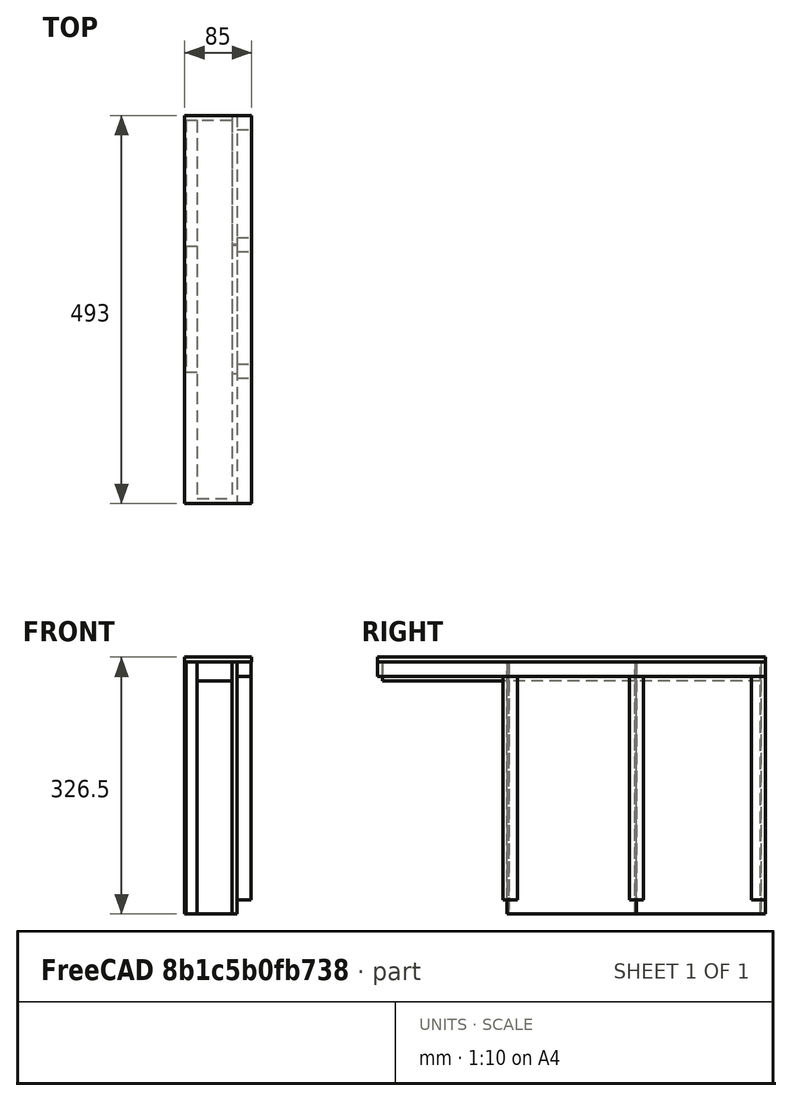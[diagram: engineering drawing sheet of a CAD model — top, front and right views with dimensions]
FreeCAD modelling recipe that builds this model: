
FCSTD DOCUMENT  (FreeCAD 0.21R33694 (Git))
Label: enclosure
License: All rights reserved
LicenseURL: http://en.wikipedia.org/wiki/All_rights_reserved
objects: PartDesign::Body×18, TechDraw::DrawViewDimension×12, PartDesign::FeatureBase×11, Sketcher::SketchObject×7, PartDesign::Pad×7, TechDraw::DrawViewPart×6, TechDraw::DrawSVGTemplate×1, TechDraw::DrawProjGroupItem×1, TechDraw::DrawProjGroup×1, TechDraw::DrawPage×1
note: 64 computed .brp shape members not serialized (recipe doc carries the construction recipe); baked Part::Feature solids carry a one-line shape summary decoded from their .brp

FEATURE [Sketcher::SketchObject] Sketch
  FullyConstrained = true
  MapMode = 5
  Placement = pos=(0,0,0) rot=(1,0,0;1.5708rad)
  Support = -> [XZ_Plane]
  sketch-geometry (6):
    g0: LineSegment StartX=0 StartY=2e-16 StartZ=0 EndX=14 EndY=2e-16 EndZ=0
    g1: LineSegment StartX=14 StartY=320 StartZ=0 EndX=0 EndY=320 EndZ=0
    g2: LineSegment StartX=0 StartY=320 StartZ=0 EndX=0 EndY=0 EndZ=0
    g3: LineSegment StartX=14 StartY=2e-16 StartZ=0 EndX=14 EndY=24 EndZ=0
    g4: LineSegment StartX=14 StartY=24 StartZ=0 EndX=14 EndY=296 EndZ=0
    g5: LineSegment StartX=14 StartY=296 StartZ=0 EndX=14 EndY=320 EndZ=0
  constraints (17):
    c: Coincident(g0,g3)
    c: Coincident(g5,g1)
    c: Coincident(g1,g2)
    c: Coincident(g2,g0)
    c: Horizontal(g0)
    c: Horizontal(g1)
    c: Vertical(g2)
    c: DistanceX(g0,g0) = 14
    c: DistanceY(g3,g5) = 320
    c: Coincident(g0,g-1)
    c: Coincident(g3,g4)
    c: Vertical(g3)
    c: Distance(g3,g0) = 24
    c: Coincident(g4,g5)
    c: Vertical(g4)
    c: Vertical(g5)
    c: Distance(g4,g1) = 24
FEATURE [PartDesign::Pad] Pad
  Direction = (0,-1,-2e-16)
  Length = 160
  Length2 = 10
  Placement = pos=(0,0,0) rot=(1,0,0;1.5708rad)
  Profile = -> Sketch
  ReferenceAxis = -> Sketch [N_Axis]
  Type = 0
FEATURE [PartDesign::Body] Body  label="p10panel_1"
  Group = -> [Sketch,Pad]
  Origin = -> Origin
  Placement = pos=(0,0,-0.5) rot=(0,0,1;0rad)
  Tip = -> Pad
FEATURE [PartDesign::FeatureBase] Clone
  BaseFeature = -> Body
FEATURE [PartDesign::Body] Body001  label="p10panel_2"
  Group = -> [Clone]
  Origin = -> Origin001
  Placement = pos=(0,160,-0.5) rot=(0,0,1;0rad)
  Tip = -> Clone
FEATURE [PartDesign::FeatureBase] Clone001
  BaseFeature = -> Body
FEATURE [PartDesign::Body] Body002  label="p10panel_3"
  Group = -> [Clone001]
  Origin = -> Origin002
  Placement = pos=(0,320,-0.5) rot=(0,0,1;0rad)
  Tip = -> Clone001
FEATURE [Sketcher::SketchObject] Sketch001
  FullyConstrained = true
  MapMode = 5
  Placement = pos=(0,0,0) rot=(1,0,0;1.5708rad)
  Support = -> [XZ_Plane003]
  sketch-geometry (4):
    g0: LineSegment StartX=0 StartY=0 StartZ=0 EndX=44 EndY=0 EndZ=0
    g1: LineSegment StartX=44 StartY=0 StartZ=0 EndX=44 EndY=24 EndZ=0
    g2: LineSegment StartX=44 StartY=24 StartZ=0 EndX=0 EndY=24 EndZ=0
    g3: LineSegment StartX=0 StartY=24 StartZ=0 EndX=0 EndY=0 EndZ=0
  constraints (11):
    c: Coincident(g0,g1)
    c: Coincident(g1,g2)
    c: Coincident(g2,g3)
    c: Coincident(g3,g0)
    c: Horizontal(g0)
    c: Horizontal(g2)
    c: Vertical(g1)
    c: Vertical(g3)
    c: DistanceX(g0,g0) = 44
    c: DistanceY(g1,g1) = 24
    c: Coincident(g0,g-1)
FEATURE [PartDesign::Pad] Pad001
  Direction = (0,-1,-2e-16)
  Length = 480
  Length2 = 10
  Placement = pos=(0,0,0) rot=(1,0,0;1.5708rad)
  Profile = -> Sketch001
  ReferenceAxis = -> Sketch001 [N_Axis]
  Type = 0
FEATURE [PartDesign::Body] Body003  label="bottomEdge"
  Group = -> [Sketch001,Pad001]
  Origin = -> Origin003
  Placement = pos=(14,319.5,-0.5) rot=(0,0,1;0rad)
  Tip = -> Pad001
FEATURE [PartDesign::FeatureBase] Clone002
  BaseFeature = -> Body003
  Placement = pos=(14,-166.5,296) rot=(0,0,1;0rad)
FEATURE [PartDesign::Body] Body004  label="topEdge"
  Group = -> [Clone002]
  Origin = -> Origin004
  Placement = pos=(0,486,-0.5) rot=(0,0,1;0rad)
  Tip = -> Clone002
FEATURE [Sketcher::SketchObject] Sketch002
  FullyConstrained = true
  MapMode = 5
  Placement = pos=(0,0,0) rot=(1,0,0;1.5708rad)
  Support = -> [XZ_Plane005]
  sketch-geometry (14):
    g0: LineSegment StartX=85 StartY=-6.5 StartZ=0 EndX=85 EndY=0 EndZ=0
    g1: LineSegment StartX=0 StartY=0 StartZ=0 EndX=0 EndY=-6.5 EndZ=0
    g2: LineSegment StartX=0 StartY=-6.5 StartZ=0 EndX=16 EndY=-6.5 EndZ=0
    g3: LineSegment StartX=16 StartY=0 StartZ=0 EndX=0 EndY=0 EndZ=0
    g4: LineSegment StartX=66.5 StartY=0 StartZ=0 EndX=60 EndY=0 EndZ=0
    g5: LineSegment StartX=85 StartY=0 StartZ=0 EndX=84.5 EndY=0 EndZ=0
    g6: LineSegment StartX=84.5 StartY=0 StartZ=0 EndX=66.5 EndY=0 EndZ=0
    g7: LineSegment StartX=84.5 StartY=-6.5 StartZ=0 EndX=85 EndY=-6.5 EndZ=0
    g8: LineSegment StartX=66.5 StartY=-6.5 StartZ=0 EndX=84.5 EndY=-6.5 EndZ=0
    g9: LineSegment StartX=60 StartY=-6.5 StartZ=0 EndX=66.5 EndY=-6.5 EndZ=0
    g10: LineSegment StartX=60 StartY=0 StartZ=0 EndX=42 EndY=0 EndZ=0
    g11: LineSegment StartX=42 StartY=0 StartZ=0 EndX=16 EndY=0 EndZ=0
    g12: LineSegment StartX=16 StartY=-6.5 StartZ=0 EndX=42 EndY=-6.5 EndZ=0
    g13: LineSegment StartX=42 StartY=-6.5 StartZ=0 EndX=60 EndY=-6.5 EndZ=0
  constraints (41):
    c: Coincident(g7,g0)
    c: Coincident(g0,g5)
    c: Coincident(g3,g1)
    c: Coincident(g1,g2)
    c: Vertical(g0)
    c: Vertical(g1)
    c: DistanceY(g0,g0) = 6.5
    c: Coincident(g3,g-1)
    c: DistanceX(g2,g7) = 85
    c: Coincident(g2,g12)
    c: Horizontal(g2)
    c: Horizontal(g3)
    c: Distance(g1,g2) = 16
    c: Distance(g1,g11) = 16
    c: Coincident(g4,g10)
    c: Coincident(g6,g4)
    c: Horizontal(g4)
    c: Coincident(g5,g6)
    c: Horizontal(g5)
    c: Horizontal(g6)
    c: Coincident(g8,g7)
    c: Horizontal(g7)
    c: Coincident(g9,g8)
    c: Horizontal(g8)
    c: Coincident(g13,g9)
    c: Horizontal(g9)
    c: Distance(g13,g8) = 6.5
    c: Horizontal(g10)
    c: Horizontal(g11)
    c: Coincident(g12,g13)
    c: Horizontal(g12)
    c: Horizontal(g13)
    c: Distance(g12,g9) = 18
    c: Distance(g3,g10) = 26
    c: Coincident(g3,g11)
    c: Coincident(g11,g10)
    c: Distance(g10,g4) = 18
    c: Distance(g4,g4) = 6.5
    c: Distance(g4,g5) = 18
    c: Distance(g2,g12) = 26
    c: Distance(g8,g7) = 18
FEATURE [PartDesign::Pad] Pad002
  Direction = (0,-1,-2e-16)
  Length = 493
  Length2 = 10
  Placement = pos=(0,0,0) rot=(1,0,0;1.5708rad)
  Profile = -> Sketch002
  ReferenceAxis = -> Sketch002 [N_Axis]
  Type = 0
FEATURE [PartDesign::Body] Body005  label="bottom"
  Group = -> [Sketch002,Pad002]
  Origin = -> Origin005
  Placement = pos=(-2,326,-0.5) rot=(0,0,1;0rad)
  Tip = -> Pad002
FEATURE [Sketcher::SketchObject] Sketch003
  FullyConstrained = true
  MapMode = 5
  Placement = pos=(0,0,0) rot=(1,0,0;1.5708rad)
  Support = -> [XZ_Plane006]
  sketch-geometry (8):
    g0: LineSegment StartX=60 StartY=0 StartZ=0 EndX=60 EndY=320 EndZ=0
    g1: LineSegment StartX=0 StartY=320 StartZ=0 EndX=0 EndY=0 EndZ=0
    g2: LineSegment StartX=16 StartY=0 StartZ=0 EndX=60 EndY=0 EndZ=0
    g3: LineSegment StartX=0 StartY=0 StartZ=0 EndX=2 EndY=0 EndZ=0
    g4: LineSegment StartX=2 StartY=0 StartZ=0 EndX=16 EndY=0 EndZ=0
    g5: LineSegment StartX=60 StartY=320 StartZ=0 EndX=16 EndY=320 EndZ=0
    g6: LineSegment StartX=16 StartY=320 StartZ=0 EndX=2 EndY=320 EndZ=0
    g7: LineSegment StartX=2 StartY=320 StartZ=0 EndX=0 EndY=320 EndZ=0
  constraints (23):
    c: Coincident(g2,g0)
    c: Coincident(g0,g5)
    c: Coincident(g7,g1)
    c: Coincident(g1,g3)
    c: Vertical(g0)
    c: Vertical(g1)
    c: DistanceX(g3,g2) = 60
    c: DistanceY(g0,g0) = 320
    c: Coincident(g3,g-1)
    c: Coincident(g4,g2)
    c: Horizontal(g2)
    c: Distance(g1,g4) = 16
    c: Coincident(g3,g4)
    c: Horizontal(g3)
    c: Horizontal(g4)
    c: Distance(g3,g1) = 2
    c: Coincident(g5,g6)
    c: Horizontal(g5)
    c: Coincident(g6,g7)
    c: Horizontal(g6)
    c: Horizontal(g7)
    c: Distance(g5,g1) = 16
    c: Distance(g6,g1) = 2
FEATURE [PartDesign::Pad] Pad003
  Direction = (0,-1,-2e-16)
  Length = 6.5
  Length2 = 10
  Placement = pos=(0,0,0) rot=(1,0,0;1.5708rad)
  Profile = -> Sketch003
  ReferenceAxis = -> Sketch003 [N_Axis]
  Type = 0
FEATURE [PartDesign::Body] Body006  label="rightSide"
  Group = -> [Sketch003,Pad003]
  Origin = -> Origin006
  Placement = pos=(-2,-160.5,-0.5) rot=(0,0,1;0rad)
  Tip = -> Pad003
FEATURE [PartDesign::FeatureBase] Clone003
  BaseFeature = -> Body006
  Placement = pos=(-2,-160,3.6e-14) rot=(0,0,1;0rad)
FEATURE [PartDesign::Body] Body007  label="leftSide"
  Group = -> [Clone003]
  Origin = -> Origin007
  Placement = pos=(0,486,-0.5) rot=(0,0,1;0rad)
  Tip = -> Clone003
FEATURE [PartDesign::FeatureBase] Clone004
  BaseFeature = -> Body005
  Placement = pos=(-2,326,-7.2e-14) rot=(0,0,1;0rad)
FEATURE [PartDesign::Body] Body008  label="top"
  Group = -> [Clone004]
  Origin = -> Origin008
  Placement = pos=(0,2.8e-14,326) rot=(0,0,1;0rad)
  Tip = -> Clone004
FEATURE [Sketcher::SketchObject] Sketch004
  FullyConstrained = true
  MapMode = 5
  Placement = pos=(0,0,0) rot=(1,0,0;1.5708rad)
  Support = -> [XZ_Plane009]
  sketch-geometry (4):
    g0: LineSegment StartX=0 StartY=0 StartZ=0 EndX=6.5 EndY=0 EndZ=0
    g1: LineSegment StartX=6.5 StartY=0 StartZ=0 EndX=6.5 EndY=320 EndZ=0
    g2: LineSegment StartX=6.5 StartY=320 StartZ=0 EndX=0 EndY=320 EndZ=0
    g3: LineSegment StartX=0 StartY=320 StartZ=0 EndX=0 EndY=0 EndZ=0
  constraints (11):
    c: Coincident(g0,g1)
    c: Coincident(g1,g2)
    c: Coincident(g2,g3)
    c: Coincident(g3,g0)
    c: Horizontal(g0)
    c: Horizontal(g2)
    c: Vertical(g1)
    c: Vertical(g3)
    c: DistanceX(g0,g0) = 6.5
    c: DistanceY(g1,g1) = 320
    c: Coincident(g0,g-1)
FEATURE [PartDesign::Pad] Pad004
  Direction = (0,-1,-2e-16)
  Length = 164.33
  Length2 = 10
  Placement = pos=(0,0,0) rot=(1,0,0;1.5708rad)
  Profile = -> Sketch004
  ReferenceAxis = -> Sketch004 [N_Axis]
  Type = 0
FEATURE [PartDesign::Body] Body009  label="back_1"
  Group = -> [Sketch004,Pad004]
  Origin = -> Origin009
  Placement = pos=(58,-2.5,-0.5) rot=(0,0,1;0rad)
  Tip = -> Pad004
FEATURE [PartDesign::FeatureBase] Clone005
  BaseFeature = -> Body009
  Placement = pos=(58,-6.2,0) rot=(0,0,1;0rad)
FEATURE [PartDesign::Body] Body010  label="back_2"
  Group = -> [Clone005]
  Origin = -> Origin010
  Placement = pos=(122.5,168,319.5) rot=(0,-1,0;3.14159rad)
  Tip = -> Clone005
FEATURE [PartDesign::FeatureBase] Clone006
  BaseFeature = -> Body009
  Placement = pos=(58,-6,1e-15) rot=(0,0,1;0rad)
FEATURE [PartDesign::Body] Body011  label="back_3"
  Group = -> [Clone006]
  Origin = -> Origin011
  Placement = pos=(-2.81e-14,332,-0.5) rot=(0,0,1;0rad)
  Tip = -> Clone006
FEATURE [Sketcher::SketchObject] Sketch005
  FullyConstrained = true
  MapMode = 5
  Placement = pos=(0,0,0) rot=(1,0,0;1.5708rad)
  Support = -> [XZ_Plane012]
  sketch-geometry (4):
    g0: LineSegment StartX=0 StartY=0 StartZ=0 EndX=18 EndY=0 EndZ=0
    g1: LineSegment StartX=18 StartY=0 StartZ=0 EndX=18 EndY=18 EndZ=0
    g2: LineSegment StartX=18 StartY=18 StartZ=0 EndX=0 EndY=18 EndZ=0
    g3: LineSegment StartX=0 StartY=18 StartZ=0 EndX=0 EndY=0 EndZ=0
  constraints (11):
    c: Coincident(g0,g1)
    c: Coincident(g1,g2)
    c: Coincident(g2,g3)
    c: Coincident(g3,g0)
    c: Horizontal(g0)
    c: Horizontal(g2)
    c: Vertical(g1)
    c: Vertical(g3)
    c: DistanceX(g0,g0) = 18
    c: DistanceY(g1,g1) = 18
    c: Coincident(g0,g-1)
FEATURE [PartDesign::Pad] Pad005
  Direction = (0,-1,-2e-16)
  Length = 493
  Length2 = 10
  Placement = pos=(0,0,0) rot=(1,0,0;1.5708rad)
  Profile = -> Sketch005
  ReferenceAxis = -> Sketch005 [N_Axis]
  Type = 0
FEATURE [PartDesign::Body] Body012  label="bottomBackEdge"
  Group = -> [Sketch005,Pad005]
  Origin = -> Origin012
  Placement = pos=(64.5,326,-0.5) rot=(0,0,1;0rad)
  Tip = -> Pad005
FEATURE [PartDesign::FeatureBase] Clone007
  BaseFeature = -> Body012
  Placement = pos=(64.5,326,0) rot=(0,0,1;0rad)
FEATURE [PartDesign::Body] Body013  label="topBackEdge"
  Group = -> [Clone007]
  Origin = -> Origin013
  Placement = pos=(0,0,301.5) rot=(0,0,1;0rad)
  Tip = -> Clone007
FEATURE [Sketcher::SketchObject] Sketch006
  FullyConstrained = true
  MapMode = 5
  Placement = pos=(0,0,0) rot=(1,0,0;1.5708rad)
  Support = -> [XZ_Plane014]
  sketch-geometry (4):
    g0: LineSegment StartX=0 StartY=284 StartZ=0 EndX=18 EndY=284 EndZ=0
    g1: LineSegment StartX=18 StartY=284 StartZ=0 EndX=18 EndY=0 EndZ=0
    g2: LineSegment StartX=18 StartY=0 StartZ=0 EndX=0 EndY=0 EndZ=0
    g3: LineSegment StartX=0 StartY=0 StartZ=0 EndX=0 EndY=284 EndZ=0
  constraints (11):
    c: Coincident(g0,g1)
    c: Coincident(g1,g2)
    c: Coincident(g2,g3)
    c: Coincident(g3,g0)
    c: Horizontal(g0)
    c: Horizontal(g2)
    c: Vertical(g1)
    c: Vertical(g3)
    c: DistanceX(g2,g2) = 18
    c: DistanceY(g1,g1) = 284
    c: Coincident(g-1,g2)
FEATURE [PartDesign::Pad] Pad006
  Direction = (0,-1,2e-16)
  Length = 18
  Length2 = 10
  Placement = pos=(0,0,0) rot=(1,0,0;1.5708rad)
  Profile = -> Sketch006
  ReferenceAxis = -> Sketch006 [N_Axis]
  Type = 0
FEATURE [PartDesign::Body] Body014  label="rightBackEdge"
  Group = -> [Sketch006,Pad006]
  Origin = -> Origin014
  Placement = pos=(64.5,-149,17.5) rot=(0,0,1;0rad)
  Tip = -> Pad006
FEATURE [PartDesign::FeatureBase] Clone008
  BaseFeature = -> Body014
  Placement = pos=(64.5,-148,17.5) rot=(0,0,1;0rad)
FEATURE [PartDesign::Body] Body015  label="leftBackEdge"
  Group = -> [Clone008]
  Origin = -> Origin015
  Placement = pos=(0,474,0) rot=(0,0,1;0rad)
  Tip = -> Clone008
FEATURE [TechDraw::DrawSVGTemplate] Template
  Height = 297
  Orientation = 0
  Template = <path>
  Width = 210
FEATURE [TechDraw::DrawProjGroupItem] ProjItem  label="Front"
  CoarseView = false
  Direction = (-0.57735,0.57735,0.57735)
  Focus = 100
  HardHidden = false
  IsoCount = 0
  IsoHidden = false
  IsoVisible = false
  LockPosition = true
  Perspective = false
  Rotation = 0
  RotationVector = (-0.707107,-0.707107,0)
  Scale = 0.2
  ScaleType = 2
  ScrubCount = 0
  SeamHidden = false
  SeamVisible = false
  SmoothHidden = false
  SmoothVisible = true
  Source = -> [Body015,Body,Body001,Body002,Body003,Body004,Body005,Body006,Body007,Body008,Body009,Body010,Body011,Body012,Body013,Body014]
  Type = 0
  X = 0
  XDirection = (-0.707107,-0.707107,0)
  Y = 0
FEATURE [TechDraw::DrawProjGroup] ProjGroup
  Anchor = -> ProjItem
  AutoDistribute = true
  LockPosition = false
  ProjectionType = 0
  Rotation = 0
  Scale = 0.2
  ScaleType = 2
  Source = -> [Body015,Body,Body001,Body002,Body003,Body004,Body005,Body006,Body007,Body008,Body009,Body010,Body011,Body012,Body013,Body014]
  Views = -> [ProjItem]
  X = 60
  Y = 241
  spacingX = 15
  spacingY = 15
FEATURE [TechDraw::DrawViewPart] View001  label="2x left/right panel"
  CoarseView = false
  Direction = (0,1,0)
  Focus = 100
  HardHidden = false
  IsoCount = 0
  IsoHidden = false
  IsoVisible = false
  LockPosition = false
  Perspective = false
  Rotation = 0
  Scale = 0.25
  ScaleType = 2
  ScrubCount = 0
  SeamHidden = false
  SeamVisible = false
  SmoothHidden = false
  SmoothVisible = true
  Source = -> [Body007]
  X = 155
  XDirection = (-1,0,0)
  Y = 51
FEATURE [TechDraw::DrawViewPart] View002  label="2x bottom/top panel"
  CoarseView = false
  Direction = (0,0,1)
  Focus = 100
  HardHidden = false
  IsoCount = 0
  IsoHidden = false
  IsoVisible = false
  LockPosition = false
  Perspective = false
  Rotation = 0
  Scale = 0.25
  ScaleType = 2
  ScrubCount = 0
  SeamHidden = false
  SeamVisible = false
  SmoothHidden = false
  SmoothVisible = true
  Source = -> [Body008]
  X = 155
  XDirection = (1,0,0)
  Y = 223
FEATURE [TechDraw::DrawViewPart] View004  label="3x back panel"
  CoarseView = false
  Direction = (1,0,0)
  Focus = 100
  HardHidden = false
  IsoCount = 0
  IsoHidden = false
  IsoVisible = false
  LockPosition = false
  Perspective = false
  Rotation = 0
  Scale = 0.25
  ScaleType = 2
  ScrubCount = 0
  SeamHidden = false
  SeamVisible = false
  SmoothHidden = false
  SmoothVisible = true
  Source = -> [Body009]
  X = 55
  XDirection = (0,1,0)
  Y = 51
FEATURE [TechDraw::DrawViewDimension] Dimension003
  AngleOverride = false
  Arbitrary = false
  ArbitraryTolerances = false
  EqualTolerance = true
  ExtensionAngle = 0
  FormatSpec = %.2w
  FormatSpecOverTolerance = %+.2w
  FormatSpecUnderTolerance = %+.2w
  Inverted = false
  LineAngle = 0
  LockPosition = false
  MeasureType = 1
  OverTolerance = 0
  References2D = -> [View002]
  Rotation = 0
  ScaleType = 1
  TheoreticalExact = false
  Type = 1
  UnderTolerance = 0
  X = -0.495893
  Y = 71.1127
FEATURE [TechDraw::DrawViewDimension] Dimension004
  AngleOverride = false
  Arbitrary = false
  ArbitraryTolerances = false
  EqualTolerance = true
  ExtensionAngle = 0
  FormatSpec = %.2w
  FormatSpecOverTolerance = %+.2w
  FormatSpecUnderTolerance = %+.2w
  Inverted = false
  LineAngle = 0
  LockPosition = false
  MeasureType = 1
  OverTolerance = 0
  References2D = -> [View001]
  Rotation = 0
  ScaleType = 1
  TheoreticalExact = false
  Type = 1
  UnderTolerance = 0
  X = -0.512282
  Y = 48.5031
FEATURE [TechDraw::DrawViewDimension] Dimension006
  AngleOverride = false
  Arbitrary = false
  ArbitraryTolerances = false
  EqualTolerance = true
  ExtensionAngle = 0
  FormatSpec = %.2w
  FormatSpecOverTolerance = %+.2w
  FormatSpecUnderTolerance = %+.2w
  Inverted = false
  LineAngle = 0
  LockPosition = false
  MeasureType = 1
  OverTolerance = 0
  References2D = -> [View004]
  Rotation = 0
  ScaleType = 1
  TheoreticalExact = false
  Type = 1
  UnderTolerance = 0
  X = -3.9584
  Y = 48.9458
FEATURE [TechDraw::DrawViewPart] View  label="2x bottom/top backEdge"
  CoarseView = false
  Direction = (1,0,0)
  Focus = 100
  HardHidden = false
  IsoCount = 0
  IsoHidden = false
  IsoVisible = false
  LockPosition = false
  Perspective = false
  Rotation = 0
  Scale = 0.25
  ScaleType = 2
  ScrubCount = 0
  SeamHidden = false
  SeamVisible = false
  SmoothHidden = false
  SmoothVisible = true
  Source = -> [Body012]
  X = 90
  XDirection = (0,1,0)
  Y = 143
FEATURE [TechDraw::DrawViewPart] View005  label="4x left/right/middleLeft/middleRight backEdge"
  CoarseView = false
  Direction = (1,0,0)
  Focus = 100
  HardHidden = false
  IsoCount = 0
  IsoHidden = false
  IsoVisible = false
  LockPosition = false
  Perspective = false
  Rotation = 90
  Scale = 0.25
  ScaleType = 2
  ScrubCount = 0
  SeamHidden = false
  SeamVisible = false
  SmoothHidden = false
  SmoothVisible = true
  Source = -> [Body014]
  X = 64
  XDirection = (0,1,0)
  Y = 170
  expr: Rotation = 90 °
FEATURE [TechDraw::DrawViewDimension] Dimension008
  AngleOverride = false
  Arbitrary = false
  ArbitraryTolerances = false
  EqualTolerance = true
  ExtensionAngle = 0
  FormatSpec = %.2w
  FormatSpecOverTolerance = %+.2w
  FormatSpecUnderTolerance = %+.2w
  Inverted = false
  LineAngle = 0
  LockPosition = false
  MeasureType = 1
  OverTolerance = 0
  References2D = -> [View005]
  Rotation = 0
  ScaleType = 1
  TheoreticalExact = false
  Type = 1
  UnderTolerance = 0
  X = -3.06326
  Y = 10.904
FEATURE [TechDraw::DrawViewDimension] Dimension010
  AngleOverride = false
  Arbitrary = false
  ArbitraryTolerances = false
  EqualTolerance = true
  ExtensionAngle = 0
  FormatSpec = %.2w
  FormatSpecOverTolerance = %+.2w
  FormatSpecUnderTolerance = %+.2w
  Inverted = false
  LineAngle = 0
  LockPosition = false
  MeasureType = 1
  OverTolerance = 0
  References2D = -> [View]
  Rotation = 0
  ScaleType = 1
  TheoreticalExact = false
  Type = 1
  UnderTolerance = 0
  X = -0.859065
  Y = 11.3821
FEATURE [TechDraw::DrawViewPart] View006  label="2x bottom/top edge"
  CoarseView = false
  Direction = (1,0,0)
  Focus = 100
  HardHidden = false
  IsoCount = 0
  IsoHidden = false
  IsoVisible = false
  LockPosition = false
  Perspective = false
  Rotation = 0
  Scale = 0.25
  ScaleType = 2
  ScrubCount = 0
  SeamHidden = false
  SeamVisible = false
  SmoothHidden = false
  SmoothVisible = true
  Source = -> [Body003]
  X = 88
  XDirection = (0,1,0)
  Y = 118
FEATURE [TechDraw::DrawViewDimension] Dimension012
  AngleOverride = false
  Arbitrary = false
  ArbitraryTolerances = false
  EqualTolerance = true
  ExtensionAngle = 0
  FormatSpec = %.2w
  FormatSpecOverTolerance = %+.2w
  FormatSpecUnderTolerance = %+.2w
  Inverted = false
  LineAngle = 0
  LockPosition = false
  MeasureType = 1
  OverTolerance = 0
  References2D = -> [View006]
  Rotation = 0
  ScaleType = 1
  TheoreticalExact = false
  Type = 1
  UnderTolerance = 0
  X = 0.17469
  Y = 12.24
FEATURE [TechDraw::DrawViewDimension] Dimension014
  AngleOverride = false
  Arbitrary = false
  ArbitraryTolerances = false
  EqualTolerance = true
  ExtensionAngle = 0
  FormatSpec = %.2w
  FormatSpecOverTolerance = %+.2w
  FormatSpecUnderTolerance = %+.2w
  Inverted = false
  LineAngle = 0
  LockPosition = false
  MeasureType = 1
  OverTolerance = 0
  References2D = -> [View004]
  Rotation = 0
  ScaleType = 1
  TheoreticalExact = false
  Type = 2
  UnderTolerance = 0
  X = -26.2527
  Y = 2.5
FEATURE [TechDraw::DrawViewDimension] Dimension015
  AngleOverride = false
  Arbitrary = false
  ArbitraryTolerances = false
  EqualTolerance = true
  ExtensionAngle = 0
  FormatSpec = %.2w
  FormatSpecOverTolerance = %+.2w
  FormatSpecUnderTolerance = %+.2w
  Inverted = false
  LineAngle = 0
  LockPosition = false
  MeasureType = 1
  OverTolerance = 0
  References2D = -> [View001]
  Rotation = 0
  ScaleType = 1
  TheoreticalExact = false
  Type = 2
  UnderTolerance = 0
  X = -13.3834
  Y = 2.36926
FEATURE [TechDraw::DrawViewDimension] Dimension
  AngleOverride = false
  Arbitrary = false
  ArbitraryTolerances = false
  EqualTolerance = true
  ExtensionAngle = 0
  FormatSpec = %.2w
  FormatSpecOverTolerance = %+.2w
  FormatSpecUnderTolerance = %+.2w
  Inverted = false
  LineAngle = 0
  LockPosition = false
  MeasureType = 1
  OverTolerance = 0
  References2D = -> [View002]
  Rotation = 0
  ScaleType = 1
  TheoreticalExact = false
  Type = 2
  UnderTolerance = 0
  X = -16.6599
  Y = 3.20173
FEATURE [TechDraw::DrawViewDimension] Dimension016
  AngleOverride = false
  Arbitrary = false
  ArbitraryTolerances = false
  EqualTolerance = true
  ExtensionAngle = 0
  FormatSpec = %.2w
  FormatSpecOverTolerance = %+.2w
  FormatSpecUnderTolerance = %+.2w
  Inverted = false
  LineAngle = 0
  LockPosition = false
  MeasureType = 1
  OverTolerance = 0
  References2D = -> [View005]
  Rotation = 0
  ScaleType = 1
  TheoreticalExact = false
  Type = 2
  UnderTolerance = 0
  X = -41.3266
  Y = 2.18786
FEATURE [TechDraw::DrawViewDimension] Dimension017
  AngleOverride = false
  Arbitrary = false
  ArbitraryTolerances = false
  EqualTolerance = true
  ExtensionAngle = 0
  FormatSpec = %.2w
  FormatSpecOverTolerance = %+.2w
  FormatSpecUnderTolerance = %+.2w
  Inverted = false
  LineAngle = 0
  LockPosition = false
  MeasureType = 1
  OverTolerance = 0
  References2D = -> [View]
  Rotation = 0
  ScaleType = 1
  TheoreticalExact = false
  Type = 2
  UnderTolerance = 0
  X = -67.1185
  Y = 2.39595
FEATURE [TechDraw::DrawViewDimension] Dimension018
  AngleOverride = false
  Arbitrary = false
  ArbitraryTolerances = false
  EqualTolerance = true
  ExtensionAngle = 0
  FormatSpec = %.2w
  FormatSpecOverTolerance = %+.2w
  FormatSpecUnderTolerance = %+.2w
  Inverted = false
  LineAngle = 0
  LockPosition = false
  MeasureType = 1
  OverTolerance = 0
  References2D = -> [View006]
  Rotation = 0
  ScaleType = 1
  TheoreticalExact = false
  Type = 2
  UnderTolerance = 0
  X = -65.8526
  Y = 3.28034
FEATURE [TechDraw::DrawPage] Page  label="components"
  KeepUpdated = true
  NextBalloonIndex = 1
  ProjectionType = 0
  Scale = 0.2
  Template = -> Template
  Views = -> [ProjGroup,View001,View002,View004,Dimension003,Dimension004,Dimension006,View,View005,Dimension008,Dimension010,View006,Dimension012,Dimension014,Dimension015,Dimension,Dimension016,Dimension017,Dimension018]
FEATURE [PartDesign::FeatureBase] Clone009
  BaseFeature = -> Body014
  Placement = pos=(64.5,-144.5,17.5) rot=(0,0,1;0rad)
FEATURE [PartDesign::Body] Body016  label="rightMiddleBackEdge"
  Group = -> [Clone009]
  Origin = -> Origin016
  Placement = pos=(0,155,0) rot=(0,0,1;0rad)
  Tip = -> Clone009
FEATURE [PartDesign::FeatureBase] Clone010
  BaseFeature = -> Body014
  Placement = pos=(64.5,-148,17.5) rot=(0,0,1;0rad)
FEATURE [PartDesign::Body] Body017  label="leftMiddleBackEdge"
  Group = -> [Clone010]
  Origin = -> Origin017
  Placement = pos=(0,319,0) rot=(0,0,1;0rad)
  Tip = -> Clone010
note: 1 file-system path scrubbed to <path> (originals preserved in the JSON sidecar)
